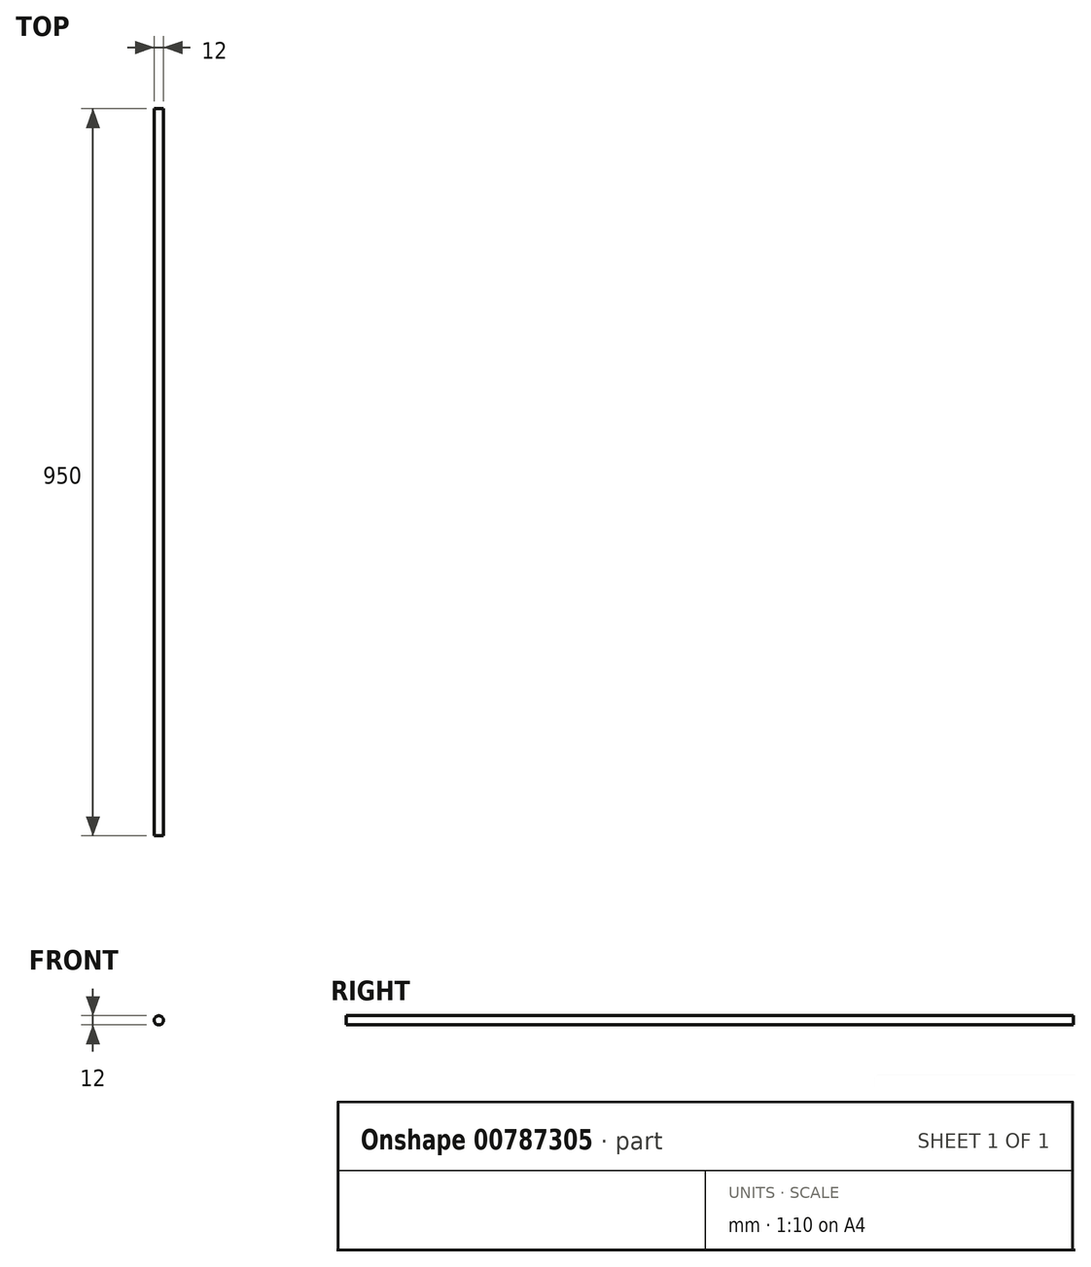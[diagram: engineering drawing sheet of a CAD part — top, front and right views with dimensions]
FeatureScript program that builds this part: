
annotation { "Feature Type Name" : "Feature", "Feature Type Description" : "" }
export const myFeature = defineFeature(function(context is Context, id is Id, definition is map)
    precondition{}
    {
        {
            var Q0;
            Q0=qCreatedBy(makeId("Front.planeOp"),FACE);
            var sketch = newSketch(context, id + "F0", { "sketchPlane" : qUnion([Q0])});
            skCircle(sketch, "E0", {"center": v(0, 0) * mm, "radius": 6 * mm});
            skSolve(sketch);
        }
        {
            var Q0;
            Q0=makeQuery(id+"F0.imprint","IMPRINT",FACE,{"disambiguationData":[TD([[makeQuery(id+"F0.imprint","IMPRINT",EDGE,{"derivedFrom":sQuery(id+"F0.wireOp",EDGE,"E0")}),1.0]])]});
            var Q1;
            Q1=sQuery(id+"F0.wireOp",EDGE,"E0");
            extrude(context, id + "F1", {"entities" : qUnion([Q0]), "surfaceEntities" : qUnion([Q1]), "depth" : (900 + 2 * 25) * mm, "offsetDistance" : 25 * mm});
        }
    });
